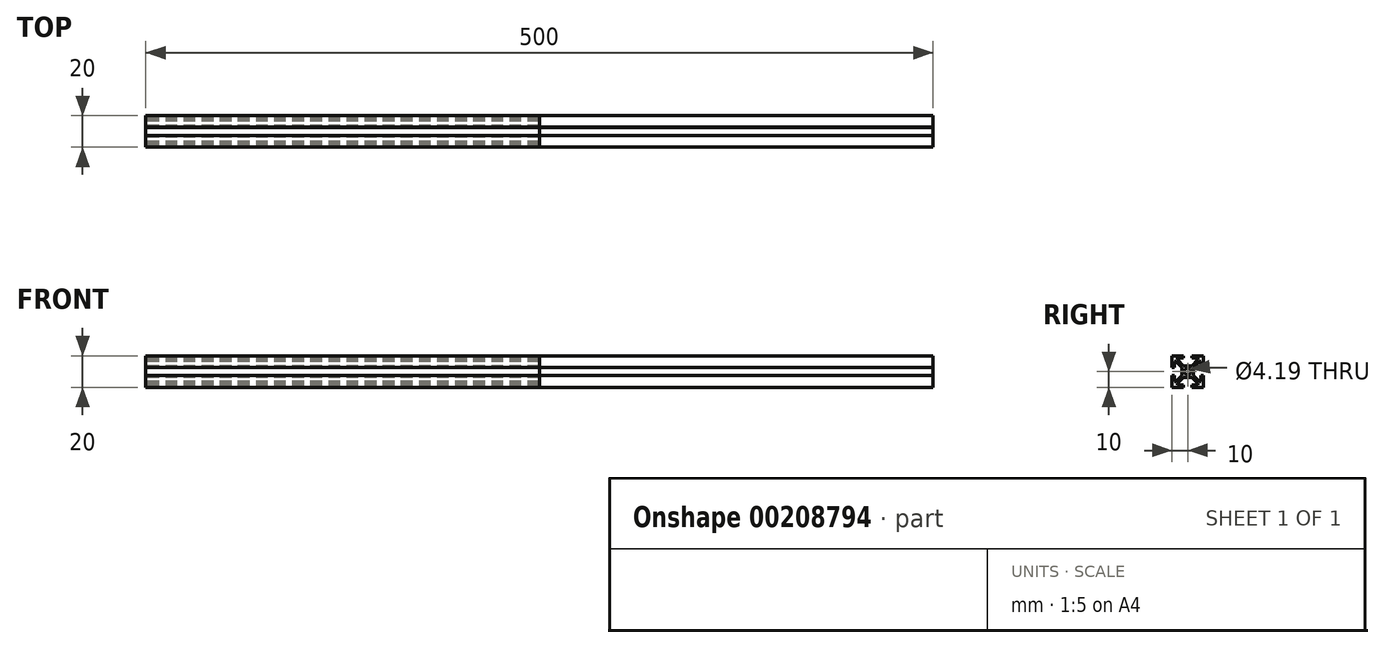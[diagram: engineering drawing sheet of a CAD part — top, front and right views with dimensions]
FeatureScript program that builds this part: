
annotation { "Feature Type Name" : "Feature", "Feature Type Description" : "" }
export const myFeature = defineFeature(function(context is Context, id is Id, definition is map)
    precondition{}
    {
        {
            var Q0;
            Q0=qCreatedBy(makeId("Right.planeOp"),FACE);
            var sketch = newSketch(context, id + "F0", { "sketchPlane" : qUnion([Q0])});
            skLineSegment(sketch, "E0.bottom", {"start": v(-20, 20) * mm, "end": v(-12.63, 20) * mm});
            skLineSegment(sketch, "E1", {"start": v(-7.37, 20) * mm, "end": v(0, 20) * mm});
            skLineSegment(sketch, "E2", {"start": v(0, 0) * mm, "end": v(-7.37, 0) * mm});
            skLineSegment(sketch, "E3", {"start": v(-12.63, 0) * mm, "end": v(-20, 0) * mm});
            skLineSegment(sketch, "E4", {"start": v(-20, 0) * mm, "end": v(-20, 7.37) * mm});
            skLineSegment(sketch, "E5", {"start": v(-20, 12.63) * mm, "end": v(-20, 20) * mm});
            skLineSegment(sketch, "E6", {"start": v(0, 0) * mm, "end": v(0, 7.37) * mm});
            skLineSegment(sketch, "E7", {"start": v(0, 12.63) * mm, "end": v(0, 20) * mm});
            skLineSegment(sketch, "E8", {"start": v(-20, 12.63) * mm, "end": v(-18.5, 12.63) * mm});
            skLineSegment(sketch, "E9", {"start": v(-18.5, 12.63) * mm, "end": v(-18.5, 16.44) * mm});
            skLineSegment(sketch, "E10", {"start": v(-18.5, 16.44) * mm, "end": v(-17.5, 16.44) * mm});
            skLineSegment(sketch, "E11", {"start": v(-17.5, 16.44) * mm, "end": v(-13.65, 12.6) * mm});
            skLineSegment(sketch, "E12", {"start": v(-12.63, 20) * mm, "end": v(-12.63, 18.5) * mm});
            skLineSegment(sketch, "E13", {"start": v(-12.63, 18.5) * mm, "end": v(-16.44, 18.5) * mm});
            skLineSegment(sketch, "E14", {"start": v(-16.44, 18.5) * mm, "end": v(-16.44, 17.5) * mm});
            skLineSegment(sketch, "E15", {"start": v(-16.44, 17.5) * mm, "end": v(-12.6, 13.65) * mm});
            skLineSegment(sketch, "E16", {"start": v(0, 0) * mm, "end": v(-20, 20) * mm, "construction": true});
            skLineSegment(sketch, "E17", {"start": v(0, 20) * mm, "end": v(-20, 0) * mm, "construction": true});
            skLineSegment(sketch, "E18", {"start": v(-20, 7.37) * mm, "end": v(-18.5, 7.37) * mm});
            skLineSegment(sketch, "E19", {"start": v(-18.5, 7.37) * mm, "end": v(-18.5, 3.56) * mm});
            skLineSegment(sketch, "E20", {"start": v(-18.5, 3.56) * mm, "end": v(-17.5, 3.56) * mm});
            skLineSegment(sketch, "E21", {"start": v(-17.5, 3.56) * mm, "end": v(-13.65, 7.4) * mm});
            skLineSegment(sketch, "E22", {"start": v(-12.63, 0) * mm, "end": v(-12.63, 1.5) * mm});
            skLineSegment(sketch, "E23", {"start": v(-12.63, 1.5) * mm, "end": v(-16.44, 1.5) * mm});
            skLineSegment(sketch, "E24", {"start": v(-16.44, 1.5) * mm, "end": v(-16.44, 2.5) * mm});
            skLineSegment(sketch, "E25", {"start": v(-16.44, 2.5) * mm, "end": v(-12.6, 6.35) * mm});
            skLineSegment(sketch, "E26", {"start": v(-7.37, 0) * mm, "end": v(-7.37, 1.5) * mm});
            skLineSegment(sketch, "E27", {"start": v(-7.37, 1.5) * mm, "end": v(-3.56, 1.5) * mm});
            skLineSegment(sketch, "E28", {"start": v(-3.56, 1.5) * mm, "end": v(-3.56, 2.5) * mm});
            skLineSegment(sketch, "E29", {"start": v(-3.56, 2.5) * mm, "end": v(-7.4, 6.35) * mm});
            skLineSegment(sketch, "E30", {"start": v(0, 7.37) * mm, "end": v(-1.5, 7.37) * mm});
            skLineSegment(sketch, "E31", {"start": v(-1.5, 7.37) * mm, "end": v(-1.5, 3.56) * mm});
            skLineSegment(sketch, "E32", {"start": v(-1.5, 3.56) * mm, "end": v(-2.5, 3.56) * mm});
            skLineSegment(sketch, "E33", {"start": v(-2.5, 3.56) * mm, "end": v(-6.35, 7.4) * mm});
            skLineSegment(sketch, "E34", {"start": v(0, 12.63) * mm, "end": v(-1.5, 12.63) * mm});
            skLineSegment(sketch, "E35", {"start": v(-1.5, 12.63) * mm, "end": v(-1.5, 16.44) * mm});
            skLineSegment(sketch, "E36", {"start": v(-1.5, 16.44) * mm, "end": v(-2.5, 16.44) * mm});
            skLineSegment(sketch, "E37", {"start": v(-2.5, 16.44) * mm, "end": v(-6.35, 12.6) * mm});
            skLineSegment(sketch, "E38", {"start": v(-7.37, 20) * mm, "end": v(-7.37, 18.5) * mm});
            skLineSegment(sketch, "E39", {"start": v(-7.37, 18.5) * mm, "end": v(-3.56, 18.5) * mm});
            skLineSegment(sketch, "E40", {"start": v(-3.56, 18.5) * mm, "end": v(-3.56, 17.5) * mm});
            skLineSegment(sketch, "E41", {"start": v(-3.56, 17.5) * mm, "end": v(-7.4, 13.65) * mm});
            skLineSegment(sketch, "E42", {"start": v(-7.4, 13.65) * mm, "end": v(-12.6, 13.65) * mm});
            skLineSegment(sketch, "E43", {"start": v(-6.34, 12.6) * mm, "end": v(-6.34, 7.4) * mm});
            skLineSegment(sketch, "E44", {"start": v(-7.4, 6.35) * mm, "end": v(-12.6, 6.35) * mm});
            skLineSegment(sketch, "E45", {"start": v(-13.65, 7.4) * mm, "end": v(-13.65, 12.6) * mm});
            skPoint(sketch, "E46", {"position": v(-10, 10) * mm});
            skSolve(sketch);
        }
        {
            var Q0;
            Q0=makeQuery(id+"F0.imprint","IMPRINT",FACE,{"disambiguationData":[TD([[makeQuery(id+"F0.imprint","IMPRINT",EDGE,{"derivedFrom":sQuery(id+"F0.wireOp",EDGE,"E0.bottom")}),-1.0]])]});
            extrude(context, id + "F1", {"entities" : qUnion([Q0]), "depth" : 500 * mm});
        }
        {
            var Q0;
            Q0=sQuery(id+"F0.wireOp",VERTEX,"E46");
            var Q1;
            Q1=makeQuery(id+"F1.opExtrude","SWEPT_BODY",BODY,{"disambiguationData":[OSD([sQuery(id+"F0.wireOp",EDGE,"E0.bottom"),sQuery(id+"F0.wireOp",EDGE,"E1"),sQuery(id+"F0.wireOp",EDGE,"E2"),sQuery(id+"F0.wireOp",EDGE,"E3"),sQuery(id+"F0.wireOp",EDGE,"E4"),sQuery(id+"F0.wireOp",EDGE,"E5"),sQuery(id+"F0.wireOp",EDGE,"E6"),sQuery(id+"F0.wireOp",EDGE,"E7"),sQuery(id+"F0.wireOp",EDGE,"E8"),sQuery(id+"F0.wireOp",EDGE,"E9"),sQuery(id+"F0.wireOp",EDGE,"E10"),sQuery(id+"F0.wireOp",EDGE,"E11"),sQuery(id+"F0.wireOp",EDGE,"E12"),sQuery(id+"F0.wireOp",EDGE,"E13"),sQuery(id+"F0.wireOp",EDGE,"E14"),sQuery(id+"F0.wireOp",EDGE,"E15"),sQuery(id+"F0.wireOp",EDGE,"E18"),sQuery(id+"F0.wireOp",EDGE,"E19"),sQuery(id+"F0.wireOp",EDGE,"E20"),sQuery(id+"F0.wireOp",EDGE,"E21"),sQuery(id+"F0.wireOp",EDGE,"E22"),sQuery(id+"F0.wireOp",EDGE,"E23"),sQuery(id+"F0.wireOp",EDGE,"E24"),sQuery(id+"F0.wireOp",EDGE,"E25"),sQuery(id+"F0.wireOp",EDGE,"E26"),sQuery(id+"F0.wireOp",EDGE,"E27"),sQuery(id+"F0.wireOp",EDGE,"E28"),sQuery(id+"F0.wireOp",EDGE,"E29"),sQuery(id+"F0.wireOp",EDGE,"E30"),sQuery(id+"F0.wireOp",EDGE,"E31"),sQuery(id+"F0.wireOp",EDGE,"E32"),sQuery(id+"F0.wireOp",EDGE,"E33"),sQuery(id+"F0.wireOp",EDGE,"E34"),sQuery(id+"F0.wireOp",EDGE,"E35"),sQuery(id+"F0.wireOp",EDGE,"E36"),sQuery(id+"F0.wireOp",EDGE,"E37"),sQuery(id+"F0.wireOp",EDGE,"E38"),sQuery(id+"F0.wireOp",EDGE,"E39"),sQuery(id+"F0.wireOp",EDGE,"E40"),sQuery(id+"F0.wireOp",EDGE,"E41"),sQuery(id+"F0.wireOp",EDGE,"E42"),sQuery(id+"F0.wireOp",EDGE,"E43"),sQuery(id+"F0.wireOp",EDGE,"E44"),sQuery(id+"F0.wireOp",EDGE,"E45")])]});
            hole(context, id + "F2", {"style" : HoleStyle.SIMPLE, "holeDiameter" : 4.2 * mm, "endStyle" : HoleEndStyle.THROUGH, "oppositeDirection" : true, "locations" : qUnion([Q0]), "scope" : qUnion([Q1])});
        }
        {
            var Q0;
            Q0=qSketchRegion(id+"F0",true);
            extrude(context, id + "F3", {"entities" : qUnion([Q0]), "depth" : 250 * mm});
        }
    });
